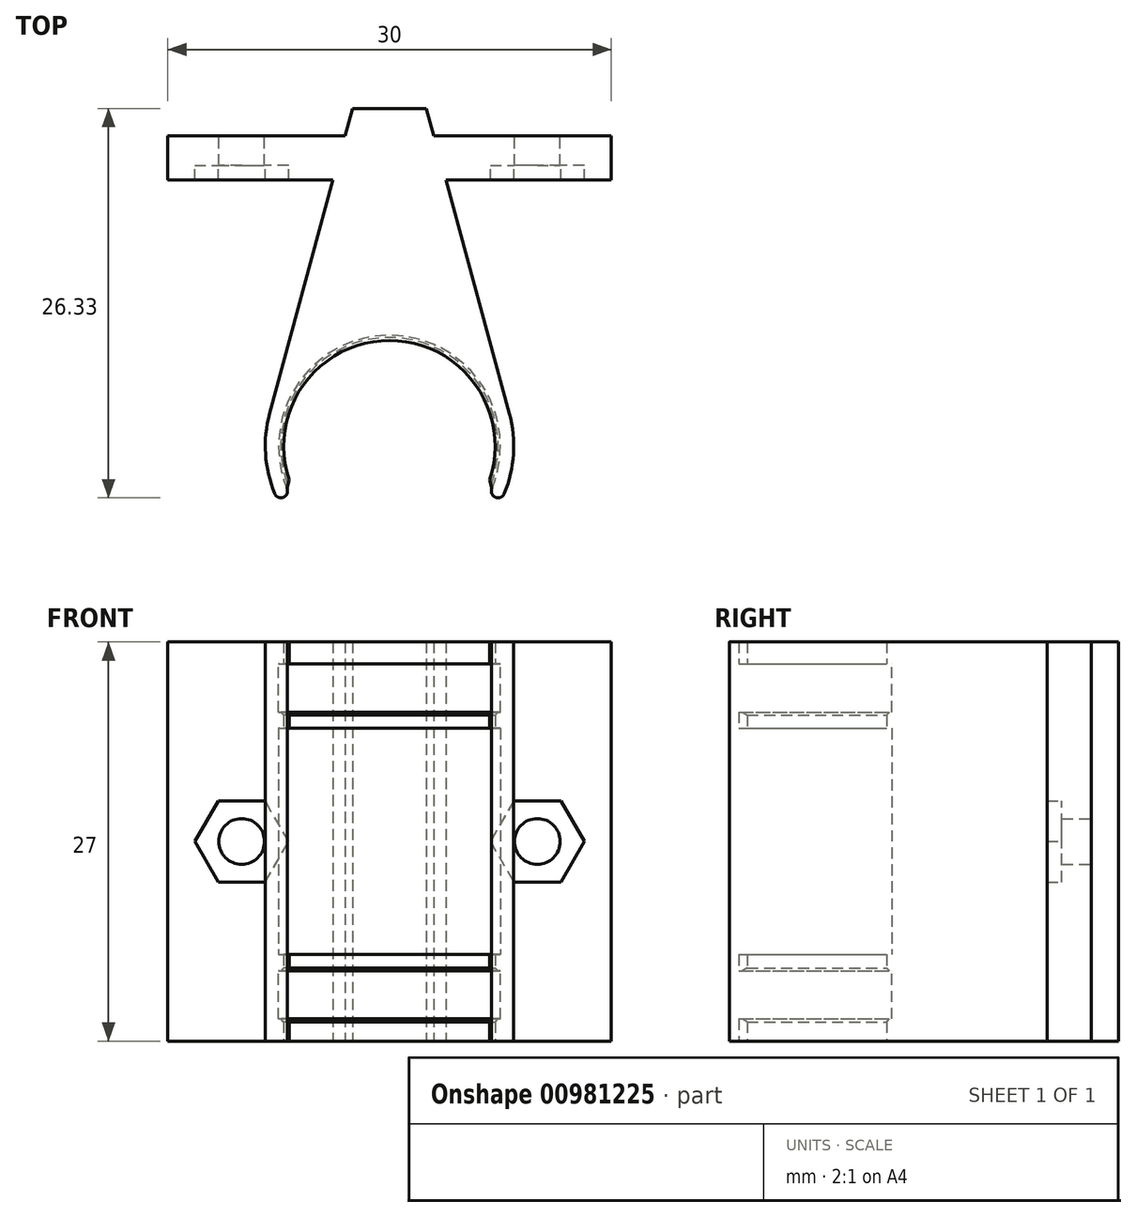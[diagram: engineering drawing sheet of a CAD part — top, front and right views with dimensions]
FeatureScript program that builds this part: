
annotation { "Feature Type Name" : "Feature", "Feature Type Description" : "" }
export const myFeature = defineFeature(function(context is Context, id is Id, definition is map)
    precondition{}
    {
        {
            var Q0;
            Q0=qCreatedBy(makeId("Top.planeOp"),FACE);
            var sketch = newSketch(context, id + "F0", { "sketchPlane" : qUnion([Q0])});
            skArc(sketch, "E0", {"start": v(6.93, -2.87) * mm, "mid": v(0, 7.5) * mm, "end": v(-6.93, -2.87) * mm});
            skArc(sketch, "E1", {"start": v(7.76, -3.21) * mm, "mid": v(0, 8.4) * mm, "end": v(-7.76, -3.21) * mm});
            skArc(sketch, "E2", {"start": v(6.77, -2.3) * mm, "mid": v(0, 7.15) * mm, "end": v(-6.77, -2.3) * mm});
            skLineSegment(sketch, "E3", {"start": v(-8.1, 2.2) * mm, "end": v(-2.5, 22.84) * mm});
            skLineSegment(sketch, "E4", {"start": v(8.1, 2.2) * mm, "end": v(2.5, 22.84) * mm});
            skLineSegment(sketch, "E5", {"start": v(-2.5, 22.84) * mm, "end": v(2.5, 22.84) * mm});
            skPoint(sketch, "E6", {"position": v(0, 22.84) * mm});
            skLineSegment(sketch, "E7", {"start": v(-3, 21) * mm, "end": v(3, 21) * mm, "construction": true});
            skLineSegment(sketch, "E8", {"start": v(-3, 21) * mm, "end": v(-15, 21) * mm});
            skLineSegment(sketch, "E9", {"start": v(-15, 21) * mm, "end": v(-15, 18) * mm});
            skLineSegment(sketch, "E10", {"start": v(-15, 18) * mm, "end": v(-3.81, 18) * mm});
            skLineSegment(sketch, "E11", {"start": v(3, 21) * mm, "end": v(15, 21) * mm});
            skLineSegment(sketch, "E12", {"start": v(15, 21) * mm, "end": v(15, 18) * mm});
            skLineSegment(sketch, "E13", {"start": v(15, 18) * mm, "end": v(3.81, 18) * mm});
            skLineSegment(sketch, "E14", {"start": v(-7.76, -3.21) * mm, "end": v(0, 0) * mm, "construction": true});
            skLineSegment(sketch, "E15", {"start": v(0, 0) * mm, "end": v(7.76, -3.21) * mm, "construction": true});
            skArc(sketch, "E16", {"start": v(7.76, -3.21) * mm, "mid": v(7.17, -3.46) * mm, "end": v(6.93, -2.87) * mm});
            skArc(sketch, "E17", {"start": v(-7.76, -3.21) * mm, "mid": v(-7.17, -3.46) * mm, "end": v(-6.93, -2.87) * mm});
            skLineSegment(sketch, "E18", {"start": v(6.93, -2.87) * mm, "end": v(6.77, -2.3) * mm});
            skLineSegment(sketch, "E19", {"start": v(-6.93, -2.87) * mm, "end": v(-6.77, -2.3) * mm});
            skSolve(sketch);
        }
        {
            var Q0;
            {var subQ0=sQuery(id+"F0.wireOp",EDGE,"E3");var subQ1=sQuery(id+"F0.wireOp",EDGE,"WnXib6kx-CsuJ-ura4-R1PZ-o8kW3uBwjOqW.top");var subQ2=makeQuery(id+"F0.imprint","INTERSECT",VERTEX,{"derivedFrom":[subQ1,subQ0]});Q0=makeQuery(id+"F0.imprint","IMPRINT",FACE,{"disambiguationData":[TD([[makeQuery(id+"F0.imprint","IMPRINT",EDGE,{"disambiguationData":[TD([[subQ2,-1.0]])],"derivedFrom":subQ1}),1.0]])]});}
            var Q1;
            {var subQ0=sQuery(id+"F0.wireOp",EDGE,"E3");var subQ1=sQuery(id+"F0.wireOp",EDGE,"WnXib6kx-CsuJ-ura4-R1PZ-o8kW3uBwjOqW.top");var subQ2=makeQuery(id+"F0.imprint","INTERSECT",VERTEX,{"derivedFrom":[subQ1,subQ0]});Q1=makeQuery(id+"F0.imprint","IMPRINT",FACE,{"disambiguationData":[TD([[makeQuery(id+"F0.imprint","IMPRINT",EDGE,{"disambiguationData":[TD([[subQ2,-1.0]])],"derivedFrom":subQ1}),-1.0]])]});}
            var Q2;
            {var subQ2=sQuery(id+"F0.wireOp",EDGE,"mogy76l5-JkOe-XnCN-tWP8-lUJ1OA8zUxDJ");var subQ6=sQuery(id+"F0.wireOp",EDGE,"E0");var subQ7=makeQuery(id+"F0.imprint","INTERSECT",VERTEX,{"disambiguationData":[OD(0.0)],"derivedFrom":[subQ6,subQ2]});Q2=makeQuery(id+"F0.imprint","IMPRINT",FACE,{"disambiguationData":[TD([[makeQuery(id+"F0.imprint","IMPRINT",EDGE,{"disambiguationData":[TD([[subQ7,-1.0]])],"derivedFrom":subQ6}),-1.0]])]});}
            var Q3;
            {var subQ0=sQuery(id+"F0.wireOp",EDGE,"mogy76l5-JkOe-XnCN-tWP8-lUJ1OA8zUxDJ");var subQ1=sQuery(id+"F0.wireOp",EDGE,"E0");var subQ2=makeQuery(id+"F0.imprint","INTERSECT",VERTEX,{"disambiguationData":[OD(0.0)],"derivedFrom":[subQ1,subQ0]});Q3=makeQuery(id+"F0.imprint","IMPRINT",FACE,{"disambiguationData":[TD([[makeQuery(id+"F0.imprint","IMPRINT",EDGE,{"disambiguationData":[TD([[subQ2,-1.0]])],"derivedFrom":subQ1}),1.0]])]});}
            var Q4;
            {var subQ0=sQuery(id+"F0.wireOp",EDGE,"E3");Q4=makeQuery(id+"F0.imprint","IMPRINT",FACE,{"disambiguationData":[TD([[makeQuery(id+"F0.imprint","IMPRINT",EDGE,{"derivedFrom":subQ0}),-1.0]])]});}
            var Q5;
            {var subQ0=sQuery(id+"F0.wireOp",EDGE,"E8");Q5=makeQuery(id+"F0.imprint","IMPRINT",FACE,{"disambiguationData":[TD([[makeQuery(id+"F0.imprint","IMPRINT",EDGE,{"derivedFrom":subQ0}),1.0]])]});}
            var Q6;
            {var subQ0=sQuery(id+"F0.wireOp",EDGE,"E11");Q6=makeQuery(id+"F0.imprint","IMPRINT",FACE,{"disambiguationData":[TD([[makeQuery(id+"F0.imprint","IMPRINT",EDGE,{"derivedFrom":subQ0}),-1.0]])]});}
            extrude(context, id + "F1", {"entities" : qUnion([Q0, Q1, Q2, Q3, Q4, Q5, Q6]), "endBound" : BoundingType.SYMMETRIC, "depth" : 27 * mm, "offsetDistance" : 25 * mm});
        }
        {
            var Q0;
            {var subQ0=sQuery(id+"F0.wireOp",EDGE,"mogy76l5-JkOe-XnCN-tWP8-lUJ1OA8zUxDJ");var subQ1=sQuery(id+"F0.wireOp",EDGE,"E0");var subQ2=makeQuery(id+"F0.imprint","INTERSECT",VERTEX,{"disambiguationData":[OD(0.0)],"derivedFrom":[subQ1,subQ0]});Q0=makeQuery(id+"F0.imprint","IMPRINT",FACE,{"disambiguationData":[TD([[makeQuery(id+"F0.imprint","IMPRINT",EDGE,{"disambiguationData":[TD([[subQ2,-1.0]])],"derivedFrom":subQ1}),1.0]])]});}
            var Q1;
            {var subQ0=sQuery(id+"F0.wireOp",EDGE,"mogy76l5-JkOe-XnCN-tWP8-lUJ1OA8zUxDJ");var subQ1=sQuery(id+"F0.wireOp",EDGE,"E0");var subQ2=makeQuery(id+"F0.imprint","INTERSECT",VERTEX,{"disambiguationData":[OD(0.0)],"derivedFrom":[subQ1,subQ0]});Q1=makeQuery(id+"F0.imprint","IMPRINT",FACE,{"disambiguationData":[TD([[makeQuery(id+"F0.imprint","IMPRINT",EDGE,{"disambiguationData":[TD([[subQ2,1.0]])],"derivedFrom":subQ1}),1.0]])]});}
            extrude(context, id + "F2", {"entities" : qUnion([Q0, Q1]), "operationType" : NewBodyOperationType.REMOVE, "endBound" : BoundingType.SYMMETRIC, "oppositeDirection" : true, "depth" : 24 * mm, "offsetDistance" : 25 * mm});
        }
        {
            var Q0;
            {var subQ0=sQuery(id+"F0.wireOp",EDGE,"mogy76l5-JkOe-XnCN-tWP8-lUJ1OA8zUxDJ");var subQ1=sQuery(id+"F0.wireOp",EDGE,"E0");var subQ2=makeQuery(id+"F0.imprint","INTERSECT",VERTEX,{"disambiguationData":[OD(0.0)],"derivedFrom":[subQ1,subQ0]});Q0=makeQuery(id+"F0.imprint","IMPRINT",FACE,{"disambiguationData":[TD([[makeQuery(id+"F0.imprint","IMPRINT",EDGE,{"disambiguationData":[TD([[subQ2,-1.0]])],"derivedFrom":subQ1}),1.0]])]});}
            extrude(context, id + "F3", {"entities" : qUnion([Q0]), "operationType" : NewBodyOperationType.ADD, "endBound" : BoundingType.SYMMETRIC, "depth" : 17.5 * mm, "offsetDistance" : 25 * mm});
        }
        {
            var Q0;
            {var subQ0=sQuery(id+"F0.wireOp",EDGE,"mogy76l5-JkOe-XnCN-tWP8-lUJ1OA8zUxDJ");var subQ1=sQuery(id+"F0.wireOp",EDGE,"E0");var subQ2=makeQuery(id+"F0.imprint","INTERSECT",VERTEX,{"disambiguationData":[OD(0.0)],"derivedFrom":[subQ1,subQ0]});Q0=makeQuery(id+"F0.imprint","IMPRINT",FACE,{"disambiguationData":[TD([[makeQuery(id+"F0.imprint","IMPRINT",EDGE,{"disambiguationData":[TD([[subQ2,-1.0]])],"derivedFrom":subQ1}),1.0]])]});}
            var Q1;
            {var subQ0=sQuery(id+"F0.wireOp",EDGE,"mogy76l5-JkOe-XnCN-tWP8-lUJ1OA8zUxDJ");var subQ1=sQuery(id+"F0.wireOp",EDGE,"E0");var subQ2=makeQuery(id+"F0.imprint","INTERSECT",VERTEX,{"disambiguationData":[OD(0.0)],"derivedFrom":[subQ1,subQ0]});Q1=makeQuery(id+"F0.imprint","IMPRINT",FACE,{"disambiguationData":[TD([[makeQuery(id+"F0.imprint","IMPRINT",EDGE,{"disambiguationData":[TD([[subQ2,1.0]])],"derivedFrom":subQ1}),1.0]])]});}
            var Q2;
            Q2=makeQuery(id+"F3.opExtrude","CAP_FACE",FACE,{"disambiguationData":[OSD([sQuery(id+"F0.wireOp",EDGE,"E0"),sQuery(id+"F0.wireOp",EDGE,"E2"),sQuery(id+"F0.wireOp",EDGE,"OyqxnQTL-80hJ-Tre8-0LPI-5BT4BykeZ9OB"),sQuery(id+"F0.wireOp",EDGE,"toQEOSAH-RIUy-FKcM-AJDC-1LW4buzCWPbQ")])],"isStart":false});
            var Q3;
            Q3=makeQuery(id+"F3.opExtrude","CAP_FACE",FACE,{"disambiguationData":[OSD([sQuery(id+"F0.wireOp",EDGE,"E0"),sQuery(id+"F0.wireOp",EDGE,"E2"),sQuery(id+"F0.wireOp",EDGE,"OyqxnQTL-80hJ-Tre8-0LPI-5BT4BykeZ9OB"),sQuery(id+"F0.wireOp",EDGE,"toQEOSAH-RIUy-FKcM-AJDC-1LW4buzCWPbQ")])],"isStart":true});
            extrude(context, id + "F4", {"entities" : qUnion([Q0, Q1]), "operationType" : NewBodyOperationType.REMOVE, "endBound" : BoundingType.UP_TO_SURFACE, "depth" : 15 * mm, "endBoundEntityFace" : qUnion([Q2]), "hasOffset" : true, "offsetDistance" : 1.1 * mm, "hasSecondDirection" : true, "secondDirectionBound" : SecondDirectionBoundingType.UP_TO_SURFACE, "secondDirectionOppositeDirection" : true, "secondDirectionDepth" : 25 * mm, "secondDirectionBoundEntityFace" : qUnion([Q3]), "hasSecondDirectionOffset" : true, "secondDirectionOffsetDistance" : 1.1 * mm});
        }
        {
            var Q0;
            Q0=makeQuery(id+"F3.opExtrude","CAP_EDGE",EDGE,{"disambiguationData":[OSD([sQuery(id+"F0.wireOp",EDGE,"E2")])],"isStart":true});
            var Q1;
            {var subQ0=sQuery(id+"F0.wireOp",EDGE,"E2");var subQ1=sQuery(id+"F0.wireOp",EDGE,"mogy76l5-JkOe-XnCN-tWP8-lUJ1OA8zUxDJ");var subQ2=sQuery(id+"F0.wireOp",EDGE,"E0");var subQ3=makeQuery(id+"F0.imprint","INTERSECT",VERTEX,{"disambiguationData":[OD(0.0)],"derivedFrom":[subQ0,subQ1]});Q1=makeQuery(id+"F4.boolean.opBoolean","COPY",EDGE,{"disambiguationData":[topologyDisambiguationEdgeConnected([makeQuery(id+"F3.opExtrude","SWEPT_FACE",FACE,{"disambiguationData":[OSD([subQ0])]})])],"derivedFrom":makeQuery(id+"F4.opExtrude","TWEAK_EDGE",EDGE,{"derivedFrom":[makeQuery(id+"F0.imprint","IMPRINT",EDGE,{"disambiguationData":[TD([[subQ3,-1.0]])],"derivedFrom":subQ0}),makeQuery(id+"F0.imprint","IMPRINT",EDGE,{"disambiguationData":[TD([[subQ3,1.0]])],"derivedFrom":subQ0}),makeQuery(id+"F3.opExtrude","CAP_FACE",FACE,{"disambiguationData":[OSD([subQ2,subQ0,subQ1])],"isStart":true})]})});}
            var Q2;
            {var subQ0=sQuery(id+"F0.wireOp",EDGE,"E2");Q2=makeQuery(id+"F2.boolean.opBoolean","COPY",EDGE,{"disambiguationData":[topologyDisambiguationEdgeConnected([makeQuery(id+"F1.opExtrude","SWEPT_FACE",FACE,{"disambiguationData":[OSD([subQ0])]})])],"derivedFrom":makeQuery(id+"F2.opExtrude","CAP_EDGE",EDGE,{"disambiguationData":[OSD([subQ0])],"isStart":false})});}
            var Q3;
            {var subQ0=sQuery(id+"F0.wireOp",EDGE,"E2");var subQ1=sQuery(id+"F0.wireOp",EDGE,"mogy76l5-JkOe-XnCN-tWP8-lUJ1OA8zUxDJ");var subQ2=sQuery(id+"F0.wireOp",EDGE,"E0");var subQ3=makeQuery(id+"F0.imprint","INTERSECT",VERTEX,{"disambiguationData":[OD(0.0)],"derivedFrom":[subQ0,subQ1]});Q3=makeQuery(id+"F4.boolean.opBoolean","COPY",EDGE,{"disambiguationData":[topologyDisambiguationEdgeConnected([makeQuery(id+"F3.opExtrude","SWEPT_FACE",FACE,{"disambiguationData":[OSD([subQ0])]})])],"derivedFrom":makeQuery(id+"F4.opExtrude","TWEAK_EDGE",EDGE,{"derivedFrom":[makeQuery(id+"F0.imprint","IMPRINT",EDGE,{"disambiguationData":[TD([[subQ3,-1.0]])],"derivedFrom":subQ0}),makeQuery(id+"F0.imprint","IMPRINT",EDGE,{"disambiguationData":[TD([[subQ3,1.0]])],"derivedFrom":subQ0}),makeQuery(id+"F3.opExtrude","CAP_FACE",FACE,{"disambiguationData":[OSD([subQ2,subQ0,subQ1])],"isStart":false})]})});}
            var Q4;
            Q4=makeQuery(id+"F3.opExtrude","CAP_EDGE",EDGE,{"disambiguationData":[OSD([sQuery(id+"F0.wireOp",EDGE,"E2")])],"isStart":false});
            var Q5;
            {var subQ0=sQuery(id+"F0.wireOp",EDGE,"E2");Q5=makeQuery(id+"F2.boolean.opBoolean","COPY",EDGE,{"disambiguationData":[topologyDisambiguationEdgeConnected([makeQuery(id+"F1.opExtrude","SWEPT_FACE",FACE,{"disambiguationData":[OSD([subQ0])]})])],"derivedFrom":makeQuery(id+"F2.opExtrude","CAP_EDGE",EDGE,{"disambiguationData":[OSD([subQ0])],"isStart":true})});}
            var Q6;
            {var subQ0=sQuery(id+"F0.wireOp",EDGE,"E2");Q6=makeQuery(id+"F2.boolean.opBoolean","COPY",EDGE,{"disambiguationData":[topologyDisambiguationEdgeConnected([makeQuery(id+"Fe5tyN9hDZ6YdIY_1.opExtrude","SWEPT_FACE",FACE,{"disambiguationData":[OSD([subQ0])]})])],"derivedFrom":makeQuery(id+"F2.opExtrude","CAP_EDGE",EDGE,{"disambiguationData":[OSD([subQ0])],"isStart":false})});}
            var Q7;
            Q7=makeQuery(id+"F6MtmlcVHjGxsjx_2.opExtrude","CAP_EDGE",EDGE,{"disambiguationData":[OSD([sQuery(id+"F0.wireOp",EDGE,"E2")])],"isStart":true});
            var Q8;
            {var subQ0=sQuery(id+"F0.wireOp",EDGE,"E2");var subQ1=sQuery(id+"F0.wireOp",EDGE,"mogy76l5-JkOe-XnCN-tWP8-lUJ1OA8zUxDJ");var subQ2=sQuery(id+"F0.wireOp",EDGE,"E0");var subQ3=makeQuery(id+"F0.imprint","INTERSECT",VERTEX,{"disambiguationData":[OD(0.0)],"derivedFrom":[subQ0,subQ1]});Q8=makeQuery(id+"F4.boolean.opBoolean","COPY",EDGE,{"disambiguationData":[topologyDisambiguationEdgeConnected([makeQuery(id+"F6MtmlcVHjGxsjx_2.opExtrude","SWEPT_FACE",FACE,{"disambiguationData":[OSD([subQ0])]})])],"derivedFrom":makeQuery(id+"F4.opExtrude","TWEAK_EDGE",EDGE,{"derivedFrom":[makeQuery(id+"F0.imprint","IMPRINT",EDGE,{"disambiguationData":[TD([[subQ3,-1.0]])],"derivedFrom":subQ0}),makeQuery(id+"F0.imprint","IMPRINT",EDGE,{"disambiguationData":[TD([[subQ3,1.0]])],"derivedFrom":subQ0}),makeQuery(id+"F3.opExtrude","CAP_FACE",FACE,{"disambiguationData":[OSD([subQ2,subQ0,subQ1])],"isStart":true})]})});}
            var Q9;
            {var subQ0=sQuery(id+"F0.wireOp",EDGE,"E2");var subQ1=sQuery(id+"F0.wireOp",EDGE,"mogy76l5-JkOe-XnCN-tWP8-lUJ1OA8zUxDJ");var subQ2=sQuery(id+"F0.wireOp",EDGE,"E0");var subQ3=makeQuery(id+"F0.imprint","INTERSECT",VERTEX,{"disambiguationData":[OD(0.0)],"derivedFrom":[subQ0,subQ1]});Q9=makeQuery(id+"F4.boolean.opBoolean","COPY",EDGE,{"disambiguationData":[topologyDisambiguationEdgeConnected([makeQuery(id+"F6MtmlcVHjGxsjx_2.opExtrude","SWEPT_FACE",FACE,{"disambiguationData":[OSD([subQ0])]})])],"derivedFrom":makeQuery(id+"F4.opExtrude","TWEAK_EDGE",EDGE,{"derivedFrom":[makeQuery(id+"F0.imprint","IMPRINT",EDGE,{"disambiguationData":[TD([[subQ3,-1.0]])],"derivedFrom":subQ0}),makeQuery(id+"F0.imprint","IMPRINT",EDGE,{"disambiguationData":[TD([[subQ3,1.0]])],"derivedFrom":subQ0}),makeQuery(id+"F3.opExtrude","CAP_FACE",FACE,{"disambiguationData":[OSD([subQ2,subQ0,subQ1])],"isStart":false})]})});}
            var Q10;
            Q10=makeQuery(id+"F6MtmlcVHjGxsjx_2.opExtrude","CAP_EDGE",EDGE,{"disambiguationData":[OSD([sQuery(id+"F0.wireOp",EDGE,"E2")])],"isStart":false});
            var Q11;
            {var subQ0=sQuery(id+"F0.wireOp",EDGE,"E2");Q11=makeQuery(id+"F2.boolean.opBoolean","COPY",EDGE,{"disambiguationData":[topologyDisambiguationEdgeConnected([makeQuery(id+"Fe5tyN9hDZ6YdIY_1.opExtrude","SWEPT_FACE",FACE,{"disambiguationData":[OSD([subQ0])]})])],"derivedFrom":makeQuery(id+"F2.opExtrude","CAP_EDGE",EDGE,{"disambiguationData":[OSD([subQ0])],"isStart":true})});}
            chamfer(context, id + "F5", {"entities" : qUnion([Q0, Q1, Q2, Q3, Q4, Q5, Q6, Q7, Q8, Q9, Q10, Q11]), "width" : .2 * mm, "tangentPropagation" : true});
        }
        {
            var Q0;
            Q0=makeQuery(id+"F1.opExtrude","SWEPT_FACE",FACE,{"disambiguationData":[OSD([sQuery(id+"F0.wireOp",EDGE,"E8")])]});
            var sketch = newSketch(context, id + "F6", { "sketchPlane" : qUnion([Q0])});
            skCircle(sketch, "E20", {"center": v(-10, 0) * mm, "radius": 1.55 * mm});
            skCircle(sketch, "E21", {"center": v(10, 0) * mm, "radius": 1.55 * mm});
            skLineSegment(sketch, "E22", {"start": v(-10, 0) * mm, "end": v(10, 0) * mm, "construction": true});
            skPoint(sketch, "E23", {"position": v(0, 0) * mm});
            skCircle(sketch, "E24.cCircle", {"center": v(-10, 0) * mm, "radius": 3.17 * mm, "construction": true});
            skLineSegment(sketch, "E24.0", {"start": v(-6.83, 0) * mm, "end": v(-8.41, -2.75) * mm});
            skLineSegment(sketch, "E24.1", {"start": v(-8.41, -2.75) * mm, "end": v(-11.59, -2.75) * mm});
            skLineSegment(sketch, "E24.2", {"start": v(-11.59, -2.75) * mm, "end": v(-13.17, 0) * mm});
            skLineSegment(sketch, "E24.3", {"start": v(-13.18, 0) * mm, "end": v(-11.59, 2.75) * mm});
            skLineSegment(sketch, "E24.4", {"start": v(-11.59, 2.75) * mm, "end": v(-8.41, 2.75) * mm});
            skLineSegment(sketch, "E24.5", {"start": v(-8.41, 2.75) * mm, "end": v(-6.82, 0) * mm});
            skCircle(sketch, "E25.cCircle", {"center": v(10, 0) * mm, "radius": 3.17 * mm, "construction": true});
            skLineSegment(sketch, "E25.0", {"start": v(6.83, 0) * mm, "end": v(8.41, 2.75) * mm});
            skLineSegment(sketch, "E25.1", {"start": v(8.41, 2.75) * mm, "end": v(11.59, 2.75) * mm});
            skLineSegment(sketch, "E25.2", {"start": v(11.59, 2.75) * mm, "end": v(13.18, 0) * mm});
            skLineSegment(sketch, "E25.3", {"start": v(13.18, 0) * mm, "end": v(11.59, -2.75) * mm});
            skLineSegment(sketch, "E25.4", {"start": v(11.59, -2.75) * mm, "end": v(8.41, -2.75) * mm});
            skLineSegment(sketch, "E25.5", {"start": v(8.41, -2.75) * mm, "end": v(6.82, 0) * mm});
            skSolve(sketch);
        }
        {
            var Q0;
            Q0=makeQuery(id+"F6.imprint","IMPRINT",FACE,{"disambiguationData":[TD([[makeQuery(id+"F6.imprint","IMPRINT",EDGE,{"derivedFrom":sQuery(id+"F6.wireOp",EDGE,"E20")}),-1.0]])]});
            var Q1;
            Q1=makeQuery(id+"F6.imprint","IMPRINT",FACE,{"disambiguationData":[TD([[makeQuery(id+"F6.imprint","IMPRINT",EDGE,{"derivedFrom":sQuery(id+"F6.wireOp",EDGE,"E20")}),1.0]])]});
            var Q2;
            Q2=makeQuery(id+"F6.imprint","IMPRINT",FACE,{"disambiguationData":[TD([[makeQuery(id+"F6.imprint","IMPRINT",EDGE,{"derivedFrom":sQuery(id+"F6.wireOp",EDGE,"E21")}),-1.0]])]});
            var Q3;
            Q3=makeQuery(id+"F6.imprint","IMPRINT",FACE,{"disambiguationData":[TD([[makeQuery(id+"F6.imprint","IMPRINT",EDGE,{"derivedFrom":sQuery(id+"F6.wireOp",EDGE,"E21")}),1.0]])]});
            var Q4;
            Q4=makeQuery(id+"F1.opExtrude","SWEPT_FACE",FACE,{"disambiguationData":[OSD([sQuery(id+"F0.wireOp",EDGE,"E13")])]});
            extrude(context, id + "F7", {"entities" : qUnion([Q0, Q1, Q2, Q3]), "operationType" : NewBodyOperationType.REMOVE, "endBound" : BoundingType.UP_TO_SURFACE, "oppositeDirection" : true, "depth" : 25 * mm, "endBoundEntityFace" : qUnion([Q4]), "offsetDistance" : 25 * mm});
        }
        {
            var Q0;
            Q0=makeQuery(id+"F6.imprint","IMPRINT",FACE,{"disambiguationData":[TD([[makeQuery(id+"F6.imprint","IMPRINT",EDGE,{"derivedFrom":sQuery(id+"F6.wireOp",EDGE,"E20")}),-1.0]])]});
            var Q1;
            Q1=makeQuery(id+"F6.imprint","IMPRINT",FACE,{"disambiguationData":[TD([[makeQuery(id+"F6.imprint","IMPRINT",EDGE,{"derivedFrom":sQuery(id+"F6.wireOp",EDGE,"E21")}),-1.0]])]});
            var Q2;
            Q2=makeQuery(id+"F1.opExtrude","SWEPT_FACE",FACE,{"disambiguationData":[OSD([sQuery(id+"F0.wireOp",EDGE,"E13")])]});
            extrude(context, id + "F8", {"entities" : qUnion([Q0, Q1]), "operationType" : NewBodyOperationType.ADD, "endBound" : BoundingType.UP_TO_SURFACE, "oppositeDirection" : true, "depth" : 25 * mm, "endBoundEntityFace" : qUnion([Q2]), "hasOffset" : true, "offsetDistance" : 1 * mm});
        }
    });
